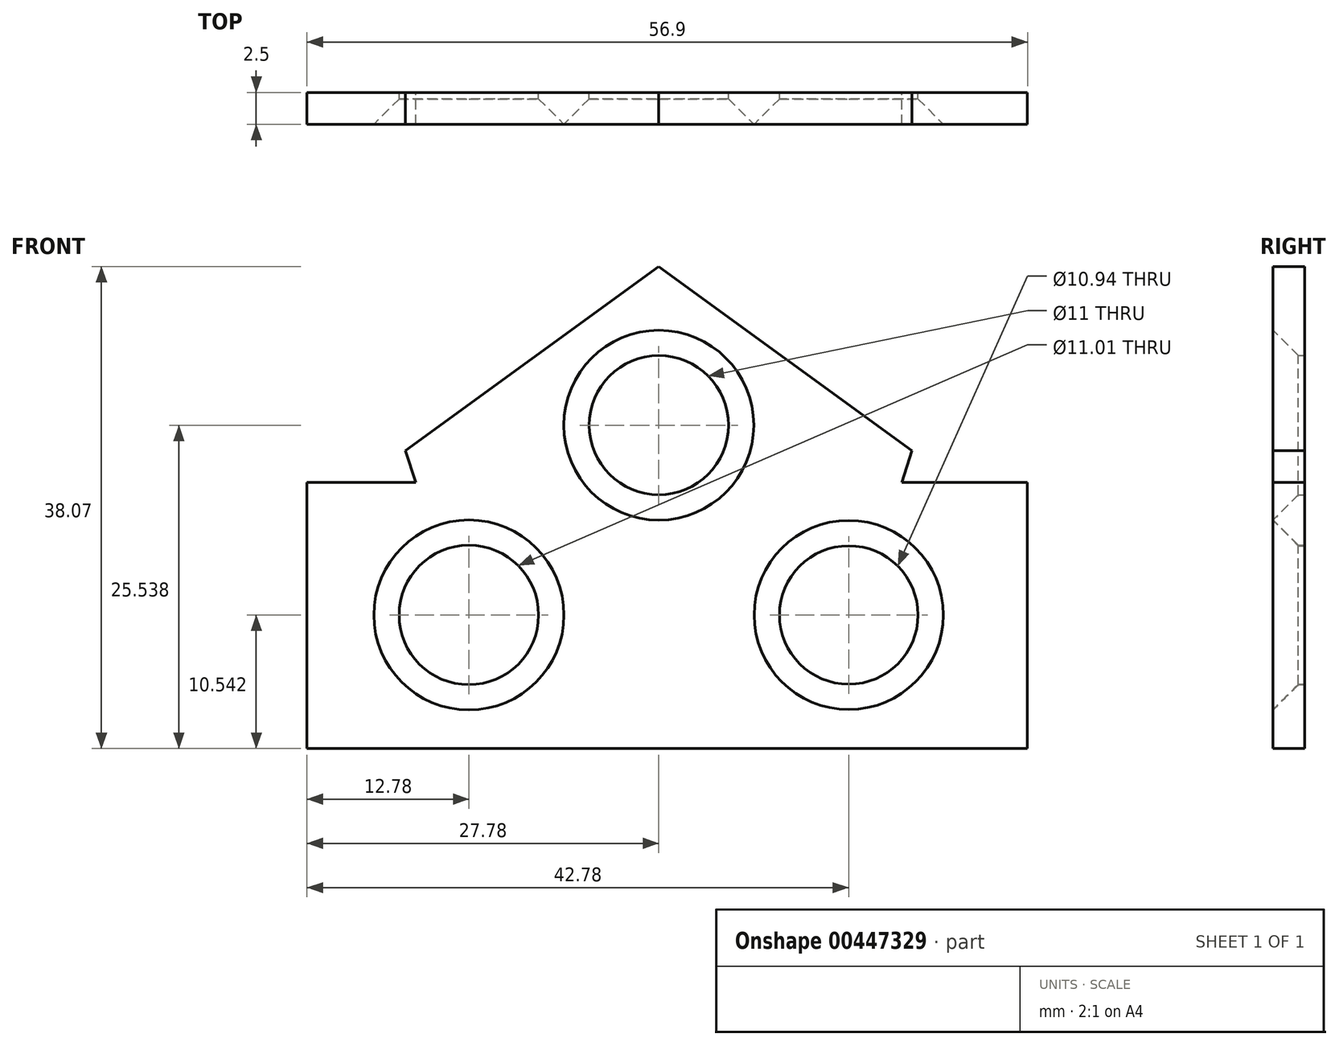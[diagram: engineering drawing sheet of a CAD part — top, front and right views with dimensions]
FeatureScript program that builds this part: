
annotation { "Feature Type Name" : "Feature", "Feature Type Description" : "" }
export const myFeature = defineFeature(function(context is Context, id is Id, definition is map)
    precondition{}
    {
        {
            var Q0;
            Q0=qCreatedBy(makeId("Front.planeOp"),FACE);
            var sketch = newSketch(context, id + "F0", { "sketchPlane" : qUnion([Q0])});
            skCircle(sketch, "E0.cCircle", {"center": v(0, 0) * mm, "radius": 21.03 * mm, "construction": true});
            skLineSegment(sketch, "E0.0", {"start": v(0, 21.03) * mm, "end": v(20, 6.5) * mm});
            skLineSegment(sketch, "E0.1", {"start": v(20, 6.5) * mm, "end": v(12.36, -17.01) * mm});
            skLineSegment(sketch, "E0.2", {"start": v(12.36, -17.01) * mm, "end": v(-12.36, -17.01) * mm});
            skLineSegment(sketch, "E0.3", {"start": v(-12.36, -17.01) * mm, "end": v(-20, 6.5) * mm});
            skLineSegment(sketch, "E0.4", {"start": v(-20, 6.5) * mm, "end": v(0, 21.03) * mm});
            skPoint(sketch, "E1", {"position": v(0, 8.5) * mm});
            skPoint(sketch, "E2", {"position": v(-15, -6.5) * mm});
            skPoint(sketch, "E3", {"position": v(15, -6.5) * mm});
            skLineSegment(sketch, "E4.bottom", {"start": v(-27.78, 3.98) * mm, "end": v(29.12, 3.98) * mm});
            skLineSegment(sketch, "E4.top", {"start": v(-27.78, -17.04) * mm, "end": v(29.12, -17.04) * mm});
            skLineSegment(sketch, "E4.left", {"start": v(-27.78, 3.98) * mm, "end": v(-27.78, -17.04) * mm});
            skLineSegment(sketch, "E4.right", {"start": v(29.12, 3.98) * mm, "end": v(29.12, -17.04) * mm});
            skCircle(sketch, "E5", {"center": v(0, 8.5) * mm, "radius": 5.5 * mm});
            skCircle(sketch, "E6", {"center": v(15, -6.5) * mm, "radius": 5.47 * mm});
            skCircle(sketch, "E7", {"center": v(-15, -6.5) * mm, "radius": 5.5 * mm});
            skSolve(sketch);
        }
        {
            var Q0;
            Q0 = qSketchRegion(id + "F0", true);
            extrude(context, id + "F1", {"entities" : qUnion([Q0]), "depth" : 2.5 * mm});
        }
        {
            var Q0;
            Q0=makeQuery(id+"F1.opExtrude","CAP_EDGE",EDGE,{"disambiguationData":[OSD([sQuery(id+"F0.wireOp",EDGE,"E5")])],"isStart":false});
            var Q1;
            Q1=makeQuery(id+"F1.opExtrude","CAP_EDGE",EDGE,{"disambiguationData":[OSD([sQuery(id+"F0.wireOp",EDGE,"E6")])],"isStart":false});
            var Q2;
            Q2=makeQuery(id+"F1.opExtrude","CAP_EDGE",EDGE,{"disambiguationData":[OSD([sQuery(id+"F0.wireOp",EDGE,"E7")])],"isStart":false});
            chamfer(context, id + "F2", {"entities" : qUnion([Q0, Q1, Q2]), "width" : 2 * mm, "tangentPropagation" : true});
        }
    });
